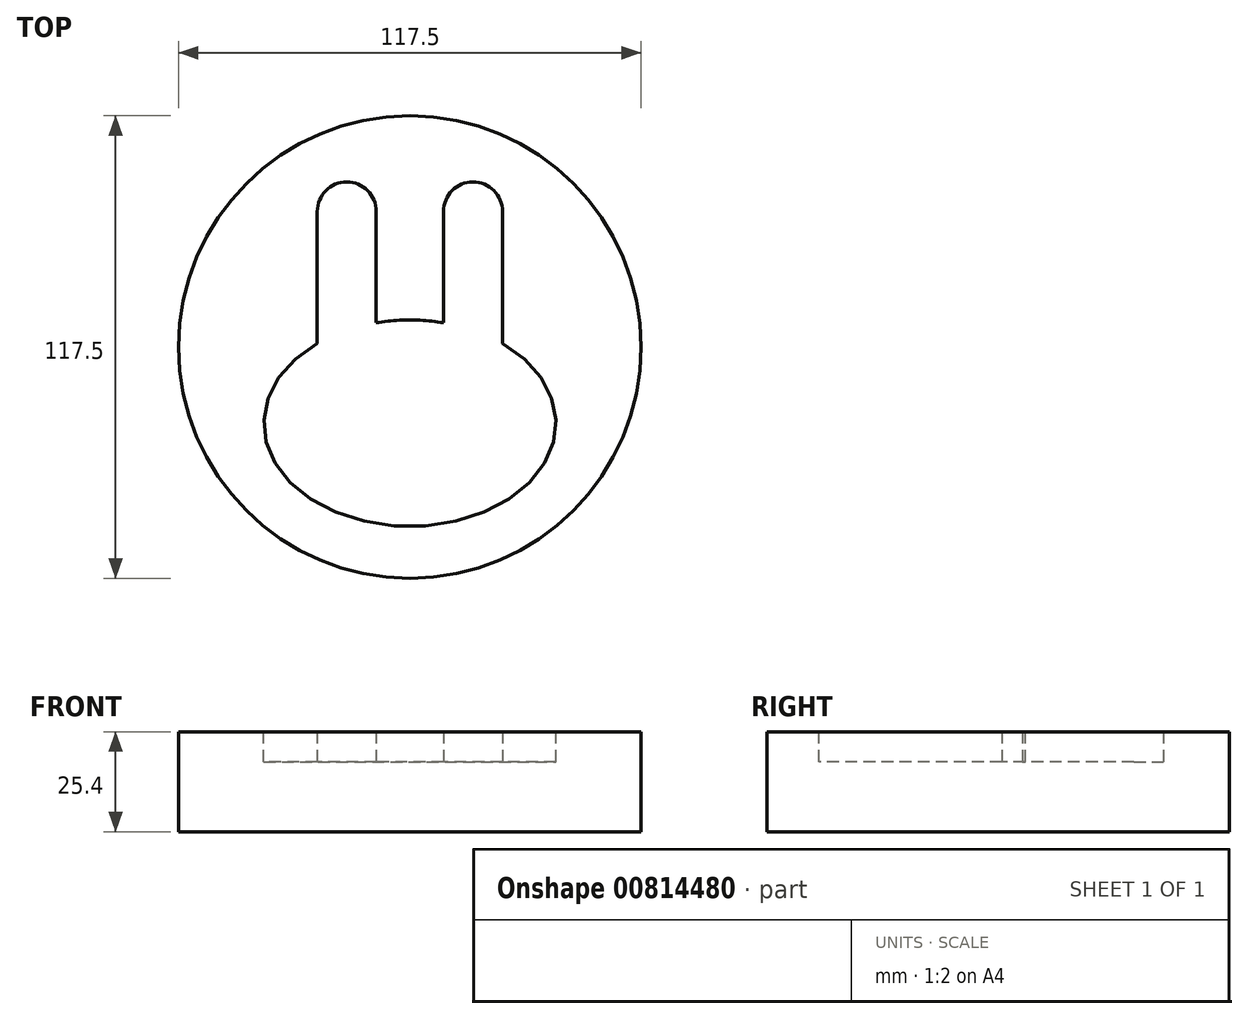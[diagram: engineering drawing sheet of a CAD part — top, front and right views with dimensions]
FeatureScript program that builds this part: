
annotation { "Feature Type Name" : "Feature", "Feature Type Description" : "" }
export const myFeature = defineFeature(function(context is Context, id is Id, definition is map)
    precondition{}
    {
        {
            var Q0;
            Q0=qCreatedBy(makeId("Top.planeOp"),FACE);
            var sketch = newSketch(context, id + "F0", { "sketchPlane" : qUnion([Q0])});
            skCircle(sketch, "E0", {"center": v(0, 0) * mm, "radius": 58.75 * mm});
            skSolve(sketch);
        }
        {
            var Q0;
            Q0=makeQuery(id+"F0.imprint","IMPRINT",FACE,{"disambiguationData":[TD([[makeQuery(id+"F0.imprint","IMPRINT",EDGE,{"derivedFrom":sQuery(id+"F0.wireOp",EDGE,"E0")}),1.0]])]});
            extrude(context, id + "F1", {"entities" : qUnion([Q0]), "depth" : 17.78 * mm, "offsetDistance" : 25.4 * mm});
        }
        {
            var Q0;
            Q0=makeQuery(id+"F1.opExtrude","CAP_FACE",FACE,{"disambiguationData":[OSD([sQuery(id+"F0.wireOp",EDGE,"E0")])],"isStart":false});
            var sketch = newSketch(context, id + "F2", { "sketchPlane" : qUnion([Q0])});
            skEllipse(sketch, "E1", {"center": v(0, -19.34) * mm, "majorRadius": 37.1 * mm, "minorRadius": 26.21 * mm, "majorAxis": v(1, 0)});
            skLineSegment(sketch, "E2.bottom", {"start": v(-23.53, 34.46) * mm, "end": v(-8.54, 34.46) * mm});
            skLineSegment(sketch, "E2.top", {"start": v(-23.53, 0) * mm, "end": v(-8.54, 0) * mm});
            skLineSegment(sketch, "E2.left", {"start": v(-23.53, 34.46) * mm, "end": v(-23.53, 0) * mm});
            skLineSegment(sketch, "E2.right", {"start": v(-8.54, 34.46) * mm, "end": v(-8.54, 0) * mm});
            skLineSegment(sketch, "E3.MirrorCS", {"start": v(8.54, 34.46) * mm, "end": v(8.54, 0) * mm});
            skLineSegment(sketch, "E4.MirrorCS", {"start": v(23.53, 34.46) * mm, "end": v(23.53, 0) * mm});
            skLineSegment(sketch, "E5.MirrorCS", {"start": v(23.53, 34.46) * mm, "end": v(8.54, 34.46) * mm});
            skLineSegment(sketch, "E6.MirrorCS", {"start": v(23.53, 0) * mm, "end": v(8.54, 0) * mm});
            skCircle(sketch, "E7", {"center": v(-16.03, 34.46) * mm, "radius": 7.5 * mm});
            skCircle(sketch, "E8", {"center": v(16.03, 34.46) * mm, "radius": 7.5 * mm});
            skSolve(sketch);
        }
        {
            var Q0;
            Q0=makeQuery(id+"F2.imprint","IMPRINT",FACE,{"disambiguationData":[TD([[makeQuery(id+"F2.imprint","IMPRINT",EDGE,{"derivedFrom":makeQuery(id+"F1.opExtrude","CAP_EDGE",EDGE,{"disambiguationData":[OSD([sQuery(id+"F0.wireOp",EDGE,"E0")])],"isStart":false})}),1.0]])]});
            extrude(context, id + "F3", {"entities" : qUnion([Q0]), "operationType" : NewBodyOperationType.ADD, "depth" : 7.62 * mm, "offsetDistance" : 25.4 * mm});
        }
    });
